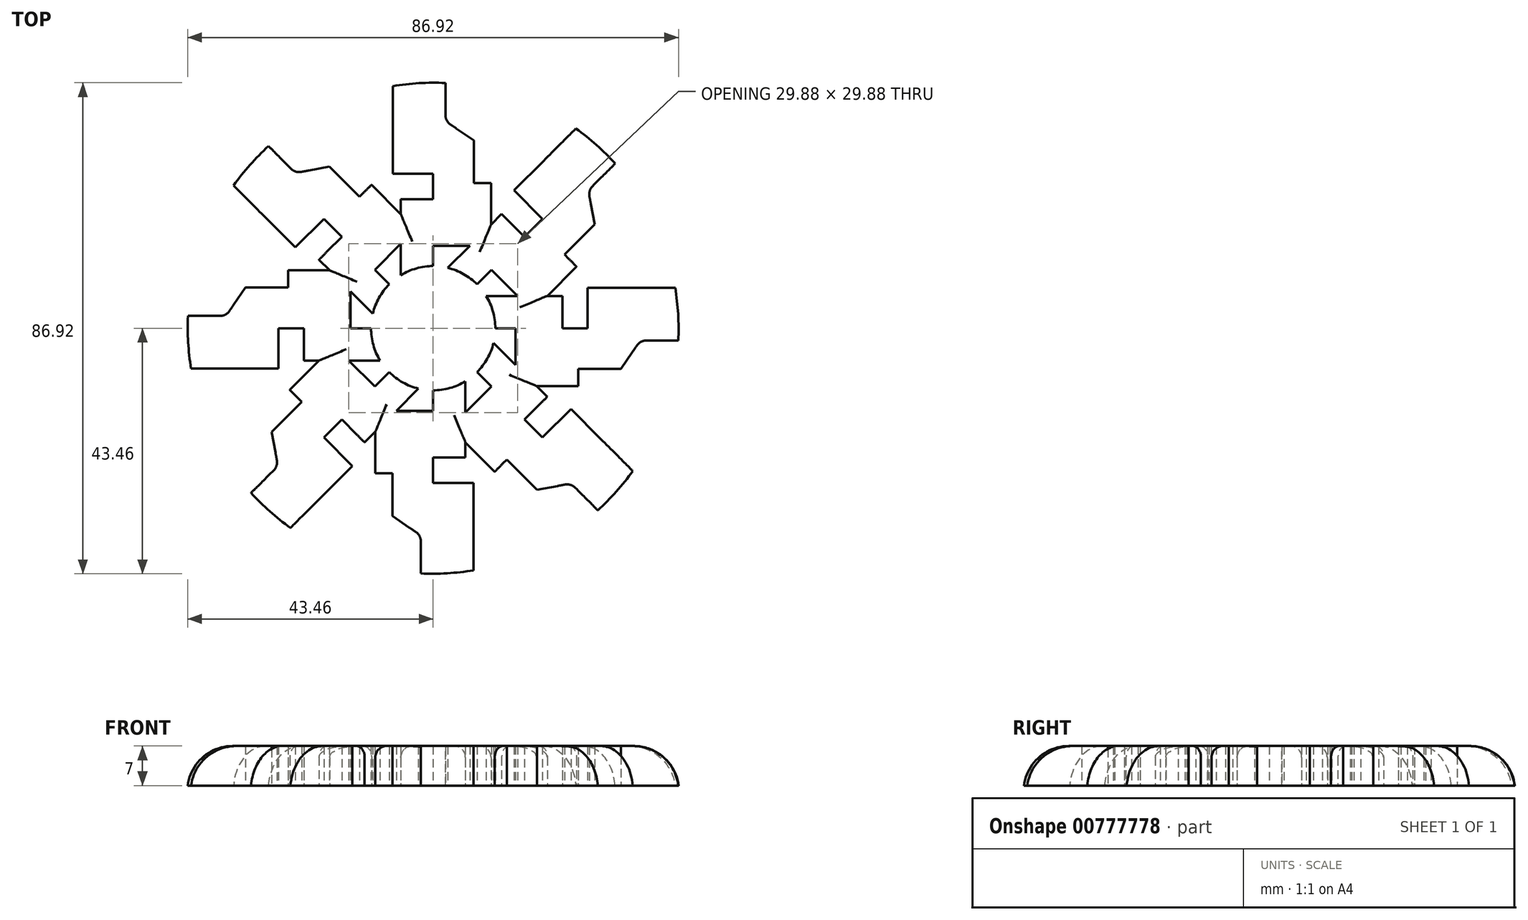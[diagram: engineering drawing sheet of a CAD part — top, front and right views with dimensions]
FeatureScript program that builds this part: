
annotation { "Feature Type Name" : "Feature", "Feature Type Description" : "" }
export const myFeature = defineFeature(function(context is Context, id is Id, definition is map)
    precondition{}
    {
        {
            var Q0;
            Q0=qCreatedBy(makeId("Top.planeOp"),FACE);
            var sketch = newSketch(context, id + "F0", { "sketchPlane" : qUnion([Q0])});
            skCircle(sketch, "E0", {"center": v(0, 0) * mm, "radius": 35 * mm});
            skCircle(sketch, "E1", {"center": v(0, 0) * mm, "radius": 11 * mm});
            skSolve(sketch);
        }
        {
            var Q0;
            Q0=qCreatedBy(makeId("Top.planeOp"),FACE);
            var sketch = newSketch(context, id + "F1", { "sketchPlane" : qUnion([Q0])});
            skLineSegment(sketch, "E2.top", {"start": v(0, 22.87) * mm, "end": v(-5.72, 22.87) * mm});
            skLineSegment(sketch, "E2.right", {"start": v(-5.72, 9.4) * mm, "end": v(-5.72, 22.87) * mm});
            skLineSegment(sketch, "E3.top", {"start": v(0, 14.6) * mm, "end": v(10.24, 14.6) * mm});
            skLineSegment(sketch, "E3.right", {"start": v(10.24, 25.67) * mm, "end": v(10.24, 14.6) * mm});
            skLineSegment(sketch, "E4.bottom", {"start": v(2.18, 36.67) * mm, "end": v(7.23, 33.25) * mm});
            skLineSegment(sketch, "E4.left", {"start": v(0, 27.37) * mm, "end": v(0, 22.87) * mm});
            skLineSegment(sketch, "E4.right", {"start": v(7.23, 33.25) * mm, "end": v(7.23, 25.67) * mm});
            skLineSegment(sketch, "E5.top", {"start": v(-7.13, 27.37) * mm, "end": v(0, 27.37) * mm});
            skPoint(sketch, "E6.orphan", {"position": v(0, 38.15) * mm});
            skLineSegment(sketch, "E7.trimOffspring", {"start": v(7.23, 25.67) * mm, "end": v(10.24, 25.67) * mm});
            skArc(sketch, "E8", {"start": v(0, 11) * mm, "mid": v(-2.97, 10.6) * mm, "end": v(-5.72, 9.4) * mm});
            skLineSegment(sketch, "E9", {"start": v(0, 14.6) * mm, "end": v(0, 11) * mm});
            skLineSegment(sketch, "E10", {"start": v(-7.13, 27.37) * mm, "end": v(-7.13, 42.87) * mm});
            skLineSegment(sketch, "E11", {"start": v(2.18, 36.67) * mm, "end": v(2.18, 43.41) * mm});
            skArc(sketch, "E12", {"start": v(2.18, 43.41) * mm, "mid": v(-2.5, 43.38) * mm, "end": v(-7.13, 42.87) * mm});
            skLineSegment(sketch, "E13.1.0", {"start": v(-16.17, 16.17) * mm, "end": v(-20.21, 12.13) * mm});
            skLineSegment(sketch, "E13.1.1", {"start": v(-10.33, 10.33) * mm, "end": v(-7.78, 7.78) * mm});
            skLineSegment(sketch, "E13.1.2", {"start": v(-18.4, 28.62) * mm, "end": v(-13.04, 23.26) * mm});
            skLineSegment(sketch, "E13.1.3", {"start": v(-10.33, 10.33) * mm, "end": v(-3.09, 17.57) * mm});
            skPoint(sketch, "E13.1.4", {"position": v(-26.98, 26.98) * mm});
            skLineSegment(sketch, "E13.1.5", {"start": v(-19.35, 19.35) * mm, "end": v(-16.17, 16.17) * mm});
            skLineSegment(sketch, "E13.1.6", {"start": v(-10.69, 2.6) * mm, "end": v(-20.21, 12.13) * mm});
            skLineSegment(sketch, "E13.1.7", {"start": v(-24.4, 14.3) * mm, "end": v(-35.36, 25.27) * mm});
            skLineSegment(sketch, "E13.1.8", {"start": v(-24.4, 27.47) * mm, "end": v(-18.4, 28.62) * mm});
            skLineSegment(sketch, "E13.1.9", {"start": v(-24.4, 27.47) * mm, "end": v(-22.7, 25.77) * mm});
            skArc(sketch, "E13.1.10", {"start": v(-29.16, 32.24) * mm, "mid": v(-32.44, 28.91) * mm, "end": v(-35.36, 25.27) * mm});
            skLineSegment(sketch, "E13.1.11", {"start": v(-10.91, 25.4) * mm, "end": v(-3.09, 17.57) * mm});
            skLineSegment(sketch, "E13.1.12", {"start": v(-24.4, 14.3) * mm, "end": v(-19.35, 19.35) * mm});
            skArc(sketch, "E13.1.13", {"start": v(-7.78, 7.78) * mm, "mid": v(-9.59, 5.39) * mm, "end": v(-10.69, 2.6) * mm});
            skLineSegment(sketch, "E13.1.14", {"start": v(-13.04, 23.26) * mm, "end": v(-10.91, 25.4) * mm});
            skLineSegment(sketch, "E13.1.15", {"start": v(-22.7, 25.77) * mm, "end": v(-29.16, 32.24) * mm});
            skLineSegment(sketch, "E13.2.0", {"start": v(-22.87, 0) * mm, "end": v(-22.87, -5.72) * mm});
            skLineSegment(sketch, "E13.2.1", {"start": v(-14.6, 0) * mm, "end": v(-11, 0) * mm});
            skLineSegment(sketch, "E13.2.2", {"start": v(-33.25, 7.23) * mm, "end": v(-25.67, 7.23) * mm});
            skLineSegment(sketch, "E13.2.3", {"start": v(-14.6, 0) * mm, "end": v(-14.6, 10.24) * mm});
            skPoint(sketch, "E13.2.4", {"position": v(-38.15, 0) * mm});
            skLineSegment(sketch, "E13.2.5", {"start": v(-27.37, 0) * mm, "end": v(-22.87, 0) * mm});
            skLineSegment(sketch, "E13.2.6", {"start": v(-9.4, -5.72) * mm, "end": v(-22.87, -5.72) * mm});
            skLineSegment(sketch, "E13.2.7", {"start": v(-27.37, -7.13) * mm, "end": v(-42.87, -7.13) * mm});
            skLineSegment(sketch, "E13.2.8", {"start": v(-36.67, 2.18) * mm, "end": v(-33.25, 7.23) * mm});
            skLineSegment(sketch, "E13.2.9", {"start": v(-36.67, 2.18) * mm, "end": v(-34.27, 2.18) * mm});
            skArc(sketch, "E13.2.10", {"start": v(-43.41, 2.18) * mm, "mid": v(-43.38, -2.5) * mm, "end": v(-42.87, -7.13) * mm});
            skLineSegment(sketch, "E13.2.11", {"start": v(-25.67, 10.24) * mm, "end": v(-14.6, 10.24) * mm});
            skLineSegment(sketch, "E13.2.12", {"start": v(-27.37, -7.13) * mm, "end": v(-27.37, 0) * mm});
            skArc(sketch, "E13.2.13", {"start": v(-11, 0) * mm, "mid": v(-10.6, -2.97) * mm, "end": v(-9.4, -5.72) * mm});
            skLineSegment(sketch, "E13.2.14", {"start": v(-25.67, 7.23) * mm, "end": v(-25.67, 10.24) * mm});
            skLineSegment(sketch, "E13.2.15", {"start": v(-34.27, 2.18) * mm, "end": v(-43.41, 2.18) * mm});
            skLineSegment(sketch, "E13.3.0", {"start": v(-16.17, -16.17) * mm, "end": v(-12.13, -20.21) * mm});
            skLineSegment(sketch, "E13.3.1", {"start": v(-10.33, -10.33) * mm, "end": v(-7.78, -7.78) * mm});
            skLineSegment(sketch, "E13.3.2", {"start": v(-28.62, -18.4) * mm, "end": v(-23.26, -13.04) * mm});
            skLineSegment(sketch, "E13.3.3", {"start": v(-10.33, -10.33) * mm, "end": v(-17.57, -3.09) * mm});
            skPoint(sketch, "E13.3.4", {"position": v(-26.98, -26.98) * mm});
            skLineSegment(sketch, "E13.3.5", {"start": v(-19.35, -19.35) * mm, "end": v(-16.17, -16.17) * mm});
            skLineSegment(sketch, "E13.3.6", {"start": v(-2.6, -10.69) * mm, "end": v(-12.13, -20.21) * mm});
            skLineSegment(sketch, "E13.3.7", {"start": v(-14.3, -24.4) * mm, "end": v(-25.27, -35.36) * mm});
            skLineSegment(sketch, "E13.3.8", {"start": v(-27.47, -24.4) * mm, "end": v(-28.62, -18.4) * mm});
            skLineSegment(sketch, "E13.3.9", {"start": v(-27.47, -24.4) * mm, "end": v(-25.77, -22.7) * mm});
            skArc(sketch, "E13.3.10", {"start": v(-32.24, -29.16) * mm, "mid": v(-28.91, -32.44) * mm, "end": v(-25.27, -35.36) * mm});
            skLineSegment(sketch, "E13.3.11", {"start": v(-25.4, -10.91) * mm, "end": v(-17.57, -3.09) * mm});
            skLineSegment(sketch, "E13.3.12", {"start": v(-14.3, -24.4) * mm, "end": v(-19.35, -19.35) * mm});
            skArc(sketch, "E13.3.13", {"start": v(-7.78, -7.78) * mm, "mid": v(-5.39, -9.59) * mm, "end": v(-2.6, -10.69) * mm});
            skLineSegment(sketch, "E13.3.14", {"start": v(-23.26, -13.04) * mm, "end": v(-25.4, -10.91) * mm});
            skLineSegment(sketch, "E13.3.15", {"start": v(-25.77, -22.7) * mm, "end": v(-32.24, -29.16) * mm});
            skLineSegment(sketch, "E13.4.0", {"start": v(0, -22.87) * mm, "end": v(5.72, -22.87) * mm});
            skLineSegment(sketch, "E13.4.1", {"start": v(0, -14.6) * mm, "end": v(0, -11) * mm});
            skLineSegment(sketch, "E13.4.2", {"start": v(-7.23, -33.25) * mm, "end": v(-7.23, -25.67) * mm});
            skLineSegment(sketch, "E13.4.3", {"start": v(0, -14.6) * mm, "end": v(-10.24, -14.6) * mm});
            skPoint(sketch, "E13.4.4", {"position": v(0, -38.15) * mm});
            skLineSegment(sketch, "E13.4.5", {"start": v(0, -27.37) * mm, "end": v(0, -22.87) * mm});
            skLineSegment(sketch, "E13.4.6", {"start": v(5.72, -9.4) * mm, "end": v(5.72, -22.87) * mm});
            skLineSegment(sketch, "E13.4.7", {"start": v(7.13, -27.37) * mm, "end": v(7.13, -42.87) * mm});
            skLineSegment(sketch, "E13.4.8", {"start": v(-2.18, -36.67) * mm, "end": v(-7.23, -33.25) * mm});
            skLineSegment(sketch, "E13.4.9", {"start": v(-2.18, -36.67) * mm, "end": v(-2.18, -34.27) * mm});
            skArc(sketch, "E13.4.10", {"start": v(-2.18, -43.41) * mm, "mid": v(2.5, -43.38) * mm, "end": v(7.13, -42.87) * mm});
            skLineSegment(sketch, "E13.4.11", {"start": v(-10.24, -25.67) * mm, "end": v(-10.24, -14.6) * mm});
            skLineSegment(sketch, "E13.4.12", {"start": v(7.13, -27.37) * mm, "end": v(0, -27.37) * mm});
            skArc(sketch, "E13.4.13", {"start": v(0, -11) * mm, "mid": v(2.97, -10.6) * mm, "end": v(5.72, -9.4) * mm});
            skLineSegment(sketch, "E13.4.14", {"start": v(-7.23, -25.67) * mm, "end": v(-10.24, -25.67) * mm});
            skLineSegment(sketch, "E13.4.15", {"start": v(-2.18, -34.27) * mm, "end": v(-2.18, -43.41) * mm});
            skLineSegment(sketch, "E13.5.0", {"start": v(16.17, -16.17) * mm, "end": v(20.21, -12.13) * mm});
            skLineSegment(sketch, "E13.5.1", {"start": v(10.33, -10.33) * mm, "end": v(7.78, -7.78) * mm});
            skLineSegment(sketch, "E13.5.2", {"start": v(18.4, -28.62) * mm, "end": v(13.04, -23.26) * mm});
            skLineSegment(sketch, "E13.5.3", {"start": v(10.33, -10.33) * mm, "end": v(3.09, -17.57) * mm});
            skPoint(sketch, "E13.5.4", {"position": v(26.98, -26.98) * mm});
            skLineSegment(sketch, "E13.5.5", {"start": v(19.35, -19.35) * mm, "end": v(16.17, -16.17) * mm});
            skLineSegment(sketch, "E13.5.6", {"start": v(10.69, -2.6) * mm, "end": v(20.21, -12.13) * mm});
            skLineSegment(sketch, "E13.5.7", {"start": v(24.4, -14.3) * mm, "end": v(35.36, -25.27) * mm});
            skLineSegment(sketch, "E13.5.8", {"start": v(24.4, -27.47) * mm, "end": v(18.4, -28.62) * mm});
            skLineSegment(sketch, "E13.5.9", {"start": v(24.4, -27.47) * mm, "end": v(22.7, -25.77) * mm});
            skArc(sketch, "E13.5.10", {"start": v(29.16, -32.24) * mm, "mid": v(32.44, -28.91) * mm, "end": v(35.36, -25.27) * mm});
            skLineSegment(sketch, "E13.5.11", {"start": v(10.91, -25.4) * mm, "end": v(3.09, -17.57) * mm});
            skLineSegment(sketch, "E13.5.12", {"start": v(24.4, -14.3) * mm, "end": v(19.35, -19.35) * mm});
            skArc(sketch, "E13.5.13", {"start": v(7.78, -7.78) * mm, "mid": v(9.59, -5.39) * mm, "end": v(10.69, -2.6) * mm});
            skLineSegment(sketch, "E13.5.14", {"start": v(13.04, -23.26) * mm, "end": v(10.91, -25.4) * mm});
            skLineSegment(sketch, "E13.5.15", {"start": v(22.7, -25.77) * mm, "end": v(29.16, -32.24) * mm});
            skLineSegment(sketch, "E13.6.0", {"start": v(22.87, 0) * mm, "end": v(22.87, 5.72) * mm});
            skLineSegment(sketch, "E13.6.1", {"start": v(14.6, 0) * mm, "end": v(11, 0) * mm});
            skLineSegment(sketch, "E13.6.2", {"start": v(33.25, -7.23) * mm, "end": v(25.67, -7.23) * mm});
            skLineSegment(sketch, "E13.6.3", {"start": v(14.6, 0) * mm, "end": v(14.6, -10.24) * mm});
            skPoint(sketch, "E13.6.4", {"position": v(38.15, 0) * mm});
            skLineSegment(sketch, "E13.6.5", {"start": v(27.37, 0) * mm, "end": v(22.87, 0) * mm});
            skLineSegment(sketch, "E13.6.6", {"start": v(9.4, 5.72) * mm, "end": v(22.87, 5.72) * mm});
            skLineSegment(sketch, "E13.6.7", {"start": v(27.37, 7.13) * mm, "end": v(42.87, 7.13) * mm});
            skLineSegment(sketch, "E13.6.8", {"start": v(36.67, -2.18) * mm, "end": v(33.25, -7.23) * mm});
            skLineSegment(sketch, "E13.6.9", {"start": v(36.67, -2.18) * mm, "end": v(34.27, -2.18) * mm});
            skArc(sketch, "E13.6.10", {"start": v(43.41, -2.18) * mm, "mid": v(43.38, 2.5) * mm, "end": v(42.87, 7.13) * mm});
            skLineSegment(sketch, "E13.6.11", {"start": v(25.67, -10.24) * mm, "end": v(14.6, -10.24) * mm});
            skLineSegment(sketch, "E13.6.12", {"start": v(27.37, 7.13) * mm, "end": v(27.37, 0) * mm});
            skArc(sketch, "E13.6.13", {"start": v(11, 0) * mm, "mid": v(10.6, 2.97) * mm, "end": v(9.4, 5.72) * mm});
            skLineSegment(sketch, "E13.6.14", {"start": v(25.67, -7.23) * mm, "end": v(25.67, -10.24) * mm});
            skLineSegment(sketch, "E13.6.15", {"start": v(34.27, -2.18) * mm, "end": v(43.41, -2.18) * mm});
            skLineSegment(sketch, "E13.7.0", {"start": v(16.17, 16.17) * mm, "end": v(12.13, 20.21) * mm});
            skLineSegment(sketch, "E13.7.1", {"start": v(10.33, 10.33) * mm, "end": v(7.78, 7.78) * mm});
            skLineSegment(sketch, "E13.7.2", {"start": v(28.62, 18.4) * mm, "end": v(23.26, 13.04) * mm});
            skLineSegment(sketch, "E13.7.3", {"start": v(10.33, 10.33) * mm, "end": v(17.57, 3.09) * mm});
            skPoint(sketch, "E13.7.4", {"position": v(26.98, 26.98) * mm});
            skLineSegment(sketch, "E13.7.5", {"start": v(19.35, 19.35) * mm, "end": v(16.17, 16.17) * mm});
            skLineSegment(sketch, "E13.7.6", {"start": v(2.6, 10.69) * mm, "end": v(12.13, 20.21) * mm});
            skLineSegment(sketch, "E13.7.7", {"start": v(14.3, 24.4) * mm, "end": v(25.27, 35.36) * mm});
            skLineSegment(sketch, "E13.7.8", {"start": v(27.47, 24.4) * mm, "end": v(28.62, 18.4) * mm});
            skLineSegment(sketch, "E13.7.9", {"start": v(27.47, 24.4) * mm, "end": v(25.77, 22.7) * mm});
            skArc(sketch, "E13.7.10", {"start": v(32.24, 29.16) * mm, "mid": v(28.91, 32.44) * mm, "end": v(25.27, 35.36) * mm});
            skLineSegment(sketch, "E13.7.11", {"start": v(25.4, 10.91) * mm, "end": v(17.57, 3.09) * mm});
            skLineSegment(sketch, "E13.7.12", {"start": v(14.3, 24.4) * mm, "end": v(19.35, 19.35) * mm});
            skArc(sketch, "E13.7.13", {"start": v(7.78, 7.78) * mm, "mid": v(5.39, 9.59) * mm, "end": v(2.6, 10.69) * mm});
            skLineSegment(sketch, "E13.7.14", {"start": v(23.26, 13.04) * mm, "end": v(25.4, 10.91) * mm});
            skLineSegment(sketch, "E13.7.15", {"start": v(25.77, 22.7) * mm, "end": v(32.24, 29.16) * mm});
            skPoint(sketch, "E14.orphan", {"position": v(2.18, 34.27) * mm});
            skSolve(sketch);
        }
        {
            var Q0;
            Q0 = qSketchRegion(id + "F1", true);
            extrude(context, id + "F2", {"entities" : qUnion([Q0]), "depth" : 7 * mm, "offsetDistance" : 25 * mm});
        }
        {
            var Q0;
            Q0=makeQuery(id+"F2.opExtrude","CAP_EDGE",EDGE,{"disambiguationData":[OSD([sQuery(id+"F1.wireOp",EDGE,"E13.3.10")])],"isStart":false});
            fillet(context, id + "F3", {"entities" : qUnion([Q0]), "radius" : 8 * mm, "tangentPropagation" : true, "allowEdgeOverflow" : false});
        }
        {
            var Q0;
            Q0=makeQuery(id+"F2.opExtrude","CAP_EDGE",EDGE,{"disambiguationData":[OSD([sQuery(id+"F1.wireOp",EDGE,"E13.5.10")])],"isStart":false});
            var Q1;
            Q1=makeQuery(id+"F2.opExtrude","CAP_EDGE",EDGE,{"disambiguationData":[OSD([sQuery(id+"F1.wireOp",EDGE,"E13.4.10")])],"isStart":false});
            var Q2;
            Q2=makeQuery(id+"F2.opExtrude","CAP_EDGE",EDGE,{"disambiguationData":[OSD([sQuery(id+"F1.wireOp",EDGE,"E13.6.10")])],"isStart":false});
            var Q3;
            Q3=makeQuery(id+"F2.opExtrude","CAP_EDGE",EDGE,{"disambiguationData":[OSD([sQuery(id+"F1.wireOp",EDGE,"E13.7.10")])],"isStart":false});
            var Q4;
            Q4=makeQuery(id+"F2.opExtrude","CAP_EDGE",EDGE,{"disambiguationData":[OSD([sQuery(id+"F1.wireOp",EDGE,"E12")])],"isStart":false});
            var Q5;
            Q5=makeQuery(id+"F2.opExtrude","CAP_EDGE",EDGE,{"disambiguationData":[OSD([sQuery(id+"F1.wireOp",EDGE,"E13.1.10")])],"isStart":false});
            var Q6;
            Q6=makeQuery(id+"F2.opExtrude","CAP_EDGE",EDGE,{"disambiguationData":[OSD([sQuery(id+"F1.wireOp",EDGE,"E13.2.10")])],"isStart":false});
            fillet(context, id + "F4", {"entities" : qUnion([Q0, Q1, Q2, Q3, Q4, Q5, Q6]), "radius" : 8 * mm, "tangentPropagation" : true, "allowEdgeOverflow" : false});
        }
        {
            var Q0;
            {var subQ0=sQuery(id+"F1.wireOp",EDGE,"E13.6.6");Q0=makeQuery(id+"F2.opExtrude","CAP_EDGE",EDGE,{"disambiguationData":[OSD([subQ0]),TDD([makeQuery(id+"F1.imprint","IMPRINT",EDGE,{"disambiguationData":[TD([[makeQuery(id+"F1.imprint","INTERSECT",VERTEX,{"derivedFrom":[sQuery(id+"F1.wireOp",EDGE,"E13.6.0"),subQ0]}),1.0]])],"derivedFrom":subQ0})])],"isStart":false});}
            var Q1;
            Q1=makeQuery(id+"F2.opExtrude","CAP_EDGE",EDGE,{"disambiguationData":[OSD([sQuery(id+"F1.wireOp",EDGE,"E13.7.11")])],"isStart":false});
            var Q2;
            Q2=makeQuery(id+"F2.opExtrude","CAP_EDGE",EDGE,{"disambiguationData":[OSD([sQuery(id+"F1.wireOp",EDGE,"E3.right")])],"isStart":false});
            var Q3;
            {var subQ0=sQuery(id+"F1.wireOp",EDGE,"E13.7.6");Q3=makeQuery(id+"F2.opExtrude","CAP_EDGE",EDGE,{"disambiguationData":[OSD([subQ0]),TDD([makeQuery(id+"F1.imprint","IMPRINT",EDGE,{"disambiguationData":[TD([[makeQuery(id+"F1.imprint","INTERSECT",VERTEX,{"derivedFrom":[sQuery(id+"F1.wireOp",EDGE,"E13.7.0"),subQ0]}),1.0]])],"derivedFrom":subQ0})])],"isStart":false});}
            var Q4;
            Q4=makeQuery(id+"F2.opExtrude","CAP_EDGE",EDGE,{"disambiguationData":[OSD([sQuery(id+"F1.wireOp",EDGE,"E13.1.11")])],"isStart":false});
            var Q5;
            {var subQ0=sQuery(id+"F1.wireOp",EDGE,"E2.right");Q5=makeQuery(id+"F2.opExtrude","CAP_EDGE",EDGE,{"disambiguationData":[OSD([subQ0]),TDD([makeQuery(id+"F1.imprint","IMPRINT",EDGE,{"disambiguationData":[TD([[makeQuery(id+"F1.imprint","INTERSECT",VERTEX,{"derivedFrom":[sQuery(id+"F1.wireOp",EDGE,"E2.top"),subQ0]}),1.0]])],"derivedFrom":subQ0})])],"isStart":false});}
            var Q6;
            Q6=makeQuery(id+"F2.opExtrude","CAP_EDGE",EDGE,{"disambiguationData":[OSD([sQuery(id+"F1.wireOp",EDGE,"E13.2.11")])],"isStart":false});
            var Q7;
            {var subQ0=sQuery(id+"F1.wireOp",EDGE,"E13.1.6");Q7=makeQuery(id+"F2.opExtrude","CAP_EDGE",EDGE,{"disambiguationData":[OSD([subQ0]),TDD([makeQuery(id+"F1.imprint","IMPRINT",EDGE,{"disambiguationData":[TD([[makeQuery(id+"F1.imprint","INTERSECT",VERTEX,{"derivedFrom":[sQuery(id+"F1.wireOp",EDGE,"E13.1.0"),subQ0]}),1.0]])],"derivedFrom":subQ0})])],"isStart":false});}
            var Q8;
            Q8=makeQuery(id+"F2.opExtrude","CAP_EDGE",EDGE,{"disambiguationData":[OSD([sQuery(id+"F1.wireOp",EDGE,"E13.3.11")])],"isStart":false});
            var Q9;
            {var subQ0=sQuery(id+"F1.wireOp",EDGE,"E13.2.6");Q9=makeQuery(id+"F2.opExtrude","CAP_EDGE",EDGE,{"disambiguationData":[OSD([subQ0]),TDD([makeQuery(id+"F1.imprint","IMPRINT",EDGE,{"disambiguationData":[TD([[makeQuery(id+"F1.imprint","INTERSECT",VERTEX,{"derivedFrom":[sQuery(id+"F1.wireOp",EDGE,"E13.2.0"),subQ0]}),1.0]])],"derivedFrom":subQ0})])],"isStart":false});}
            var Q10;
            {var subQ0=sQuery(id+"F1.wireOp",EDGE,"E13.3.6");Q10=makeQuery(id+"F2.opExtrude","CAP_EDGE",EDGE,{"disambiguationData":[OSD([subQ0]),TDD([makeQuery(id+"F1.imprint","IMPRINT",EDGE,{"disambiguationData":[TD([[makeQuery(id+"F1.imprint","INTERSECT",VERTEX,{"derivedFrom":[sQuery(id+"F1.wireOp",EDGE,"E13.3.0"),subQ0]}),1.0]])],"derivedFrom":subQ0})])],"isStart":false});}
            var Q11;
            Q11=makeQuery(id+"F2.opExtrude","CAP_EDGE",EDGE,{"disambiguationData":[OSD([sQuery(id+"F1.wireOp",EDGE,"E13.4.11")])],"isStart":false});
            var Q12;
            {var subQ0=sQuery(id+"F1.wireOp",EDGE,"E13.4.6");Q12=makeQuery(id+"F2.opExtrude","CAP_EDGE",EDGE,{"disambiguationData":[OSD([subQ0]),TDD([makeQuery(id+"F1.imprint","IMPRINT",EDGE,{"disambiguationData":[TD([[makeQuery(id+"F1.imprint","INTERSECT",VERTEX,{"derivedFrom":[sQuery(id+"F1.wireOp",EDGE,"E13.4.0"),subQ0]}),1.0]])],"derivedFrom":subQ0})])],"isStart":false});}
            var Q13;
            Q13=makeQuery(id+"F2.opExtrude","CAP_EDGE",EDGE,{"disambiguationData":[OSD([sQuery(id+"F1.wireOp",EDGE,"E13.5.11")])],"isStart":false});
            var Q14;
            Q14=makeQuery(id+"F2.opExtrude","CAP_EDGE",EDGE,{"disambiguationData":[OSD([sQuery(id+"F1.wireOp",EDGE,"E13.6.11")])],"isStart":false});
            var Q15;
            {var subQ0=sQuery(id+"F1.wireOp",EDGE,"E13.5.6");Q15=makeQuery(id+"F2.opExtrude","CAP_EDGE",EDGE,{"disambiguationData":[OSD([subQ0]),TDD([makeQuery(id+"F1.imprint","IMPRINT",EDGE,{"disambiguationData":[TD([[makeQuery(id+"F1.imprint","INTERSECT",VERTEX,{"derivedFrom":[sQuery(id+"F1.wireOp",EDGE,"E13.5.0"),subQ0]}),1.0]])],"derivedFrom":subQ0})])],"isStart":false});}
            fillet(context, id + "F5", {"entities" : qUnion([Q0, Q1, Q2, Q3, Q4, Q5, Q6, Q7, Q8, Q9, Q10, Q11, Q12, Q13, Q14, Q15]), "radius" : 2 * mm, "tangentPropagation" : true, "allowEdgeOverflow" : false});
        }
        {
            var Q0;
            Q0=makeQuery(id+"F2.opExtrude","SWEPT_EDGE",EDGE,{"disambiguationData":[OSD([sQuery(id+"F1.wireOp",EDGE,"E13.2.8"),sQuery(id+"F1.wireOp",EDGE,"E13.2.15")])]});
            var Q1;
            Q1=makeQuery(id+"F2.opExtrude","SWEPT_EDGE",EDGE,{"disambiguationData":[OSD([sQuery(id+"F1.wireOp",EDGE,"E13.1.8"),sQuery(id+"F1.wireOp",EDGE,"E13.1.15")])]});
            var Q2;
            Q2=makeQuery(id+"F2.opExtrude","SWEPT_EDGE",EDGE,{"disambiguationData":[OSD([sQuery(id+"F1.wireOp",EDGE,"E4.bottom"),sQuery(id+"F1.wireOp",EDGE,"E11")])]});
            var Q3;
            Q3=makeQuery(id+"F2.opExtrude","SWEPT_EDGE",EDGE,{"disambiguationData":[OSD([sQuery(id+"F1.wireOp",EDGE,"E13.7.8"),sQuery(id+"F1.wireOp",EDGE,"E13.7.15")])]});
            var Q4;
            Q4=makeQuery(id+"F2.opExtrude","SWEPT_EDGE",EDGE,{"disambiguationData":[OSD([sQuery(id+"F1.wireOp",EDGE,"E13.6.8"),sQuery(id+"F1.wireOp",EDGE,"E13.6.15")])]});
            var Q5;
            Q5=makeQuery(id+"F2.opExtrude","SWEPT_EDGE",EDGE,{"disambiguationData":[OSD([sQuery(id+"F1.wireOp",EDGE,"E13.5.8"),sQuery(id+"F1.wireOp",EDGE,"E13.5.15")])]});
            var Q6;
            Q6=makeQuery(id+"F2.opExtrude","SWEPT_EDGE",EDGE,{"disambiguationData":[OSD([sQuery(id+"F1.wireOp",EDGE,"E13.4.8"),sQuery(id+"F1.wireOp",EDGE,"E13.4.15")])]});
            var Q7;
            Q7=makeQuery(id+"F2.opExtrude","SWEPT_EDGE",EDGE,{"disambiguationData":[OSD([sQuery(id+"F1.wireOp",EDGE,"E13.3.8"),sQuery(id+"F1.wireOp",EDGE,"E13.3.15")])]});
            fillet(context, id + "F6", {"entities" : qUnion([Q0, Q1, Q2, Q3, Q4, Q5, Q6, Q7]), "radius" : 2 * mm, "tangentPropagation" : true, "allowEdgeOverflow" : false});
        }
    });
